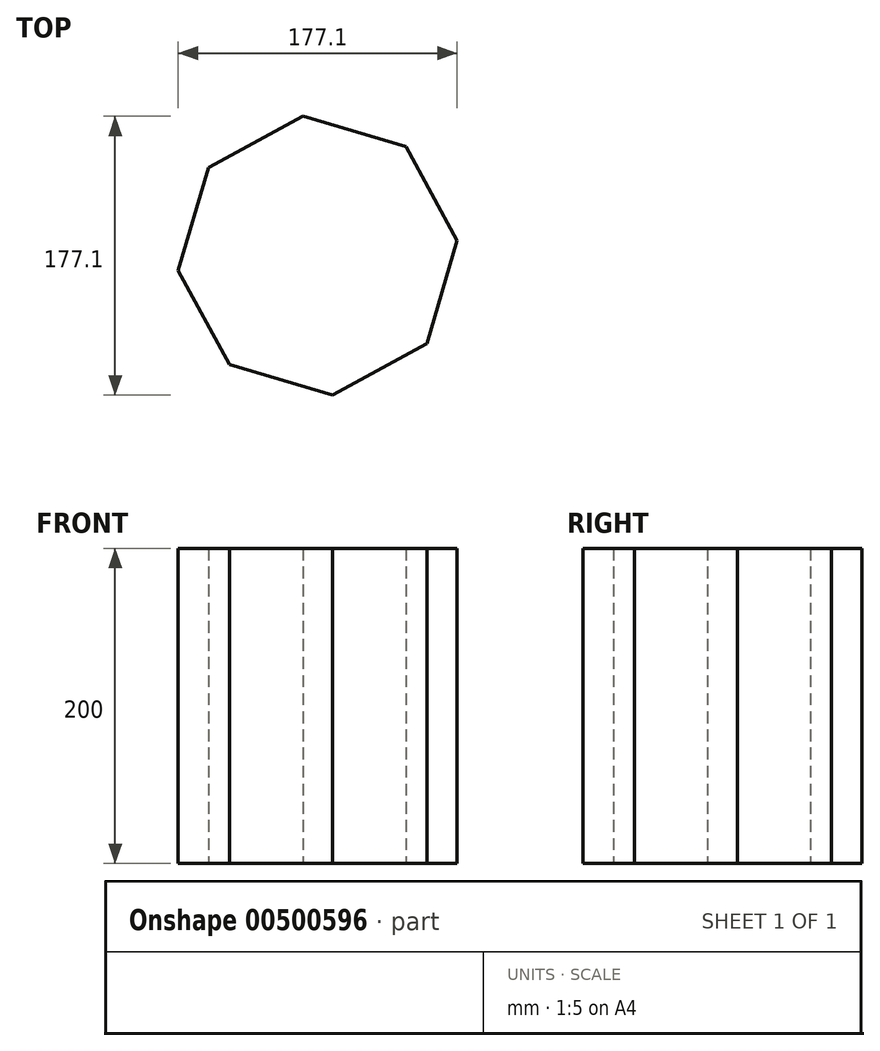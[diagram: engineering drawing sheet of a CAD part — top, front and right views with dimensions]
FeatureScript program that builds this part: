
annotation { "Feature Type Name" : "Feature", "Feature Type Description" : "" }
export const myFeature = defineFeature(function(context is Context, id is Id, definition is map)
    precondition{}
    {
        {
            var Q0;
            Q0=qCreatedBy(makeId("Top.planeOp"),FACE);
            var sketch = newSketch(context, id + "F0", { "sketchPlane" : qUnion([Q0])});
            skCircle(sketch, "E0.cCircle", {"center": v(0, 0) * mm, "radius": 89.05 * mm, "construction": true});
            skLineSegment(sketch, "E0.0", {"start": v(69.26, -55.97) * mm, "end": v(9.4, -88.55) * mm});
            skLineSegment(sketch, "E0.1", {"start": v(9.4, -88.55) * mm, "end": v(-55.97, -69.26) * mm});
            skLineSegment(sketch, "E0.2", {"start": v(-55.97, -69.26) * mm, "end": v(-88.55, -9.4) * mm});
            skLineSegment(sketch, "E0.3", {"start": v(-88.55, -9.4) * mm, "end": v(-69.26, 55.97) * mm});
            skLineSegment(sketch, "E0.4", {"start": v(-69.26, 55.97) * mm, "end": v(-9.4, 88.55) * mm});
            skLineSegment(sketch, "E0.5", {"start": v(-9.4, 88.55) * mm, "end": v(55.97, 69.26) * mm});
            skLineSegment(sketch, "E0.6", {"start": v(55.97, 69.26) * mm, "end": v(88.55, 9.4) * mm});
            skLineSegment(sketch, "E0.7", {"start": v(88.55, 9.4) * mm, "end": v(69.26, -55.97) * mm});
            skSolve(sketch);
        }
        {
            var Q0;
            Q0=makeQuery(id+"F0.imprint","IMPRINT",FACE,{"disambiguationData":[TD([[makeQuery(id+"F0.imprint","IMPRINT",EDGE,{"derivedFrom":sQuery(id+"F0.wireOp",EDGE,"E0.0")}),-1.0]])]});
            extrude(context, id + "F1", {"entities" : qUnion([Q0]), "depth" : 200 * mm});
        }
    });
